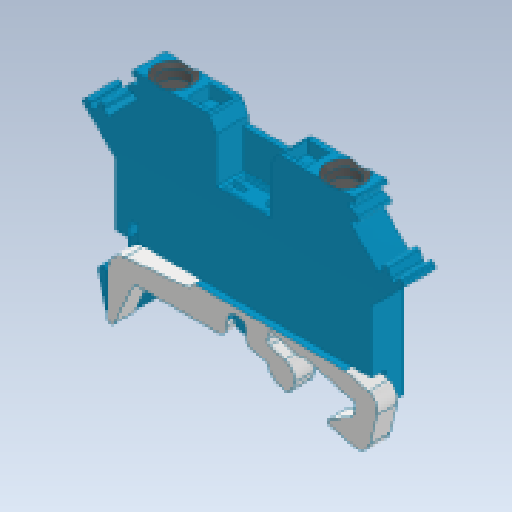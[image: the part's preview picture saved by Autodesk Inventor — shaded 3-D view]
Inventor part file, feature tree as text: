
AUTODESK INVENTOR PART (.ipt)
format: ipt  version: 2025.2 (Build 292293000, 293)  size: 807,424 bytes
history: native  units: mm
features: other x130, sketch x12, extrude x10, hole x2
ambient origin geometry x8: Origin, YZ Plane, XZ Plane, XY Plane, X Axis, Y Axis, Z Axis, Center Point
bodies: Solid1 (feature_tree)
feature tree (154):
  extrude  "Extrusion1"  Depth=2.1mm TaperAngle=0.0deg
  extrude  "Extrusion2"  Depth=2.0mm TaperAngle=0.0deg
  extrude  "Extrusion3"  Depth=7.0mm TaperAngle=0.0deg
  extrude  "Extrusion4"  Depth=5.0mm TaperAngle=0.0deg
  extrude  "Extrusion5"  Depth=3.6mm TaperAngle=0.0deg
  extrude  "Extrusion6"  TaperAngle=0.0deg  [1 undecoded]
  extrude  "Extrusion7"  TaperAngle=0.0deg  [1 undecoded]
  extrude  "Extrusion8"  TaperAngle=0.0deg  [1 undecoded]
  hole  "Hole1"  [1 undecoded]
  hole  "Hole2"  [1 undecoded]
  extrude  "Extrusion9"  Depth=10.0mm
  extrude  "Extrusion10"  Depth=10.0mm
  other  "1_2_XY"
  other  "1_2_YZ"
  other  "1_2_ZX"
  other  "1_2_X"
  other  "1_2_Y"
  other  "1_2_Z"
  other  "1_2_Center"
  other  "1_3_XY"
  other  "1_3_YZ"
  other  "1_3_ZX"
  other  "1_3_X"
  other  "1_3_Y"
  other  "1_3_Z"
  other  "1_3_Center"
  other  "1_4_XY"
  other  "1_4_YZ"
  other  "1_4_ZX"
  other  "1_4_X"
  other  "1_4_Y"
  other  "1_4_Z"
  other  "1_4_Center"
  other  "1_5_XY"
  other  "1_5_YZ"
  other  "1_5_ZX"
  other  "1_5_X"
  other  "1_5_Y"
  other  "1_5_Z"
  other  "1_5_Center"
  other  "1_6_XY"
  other  "1_6_YZ"
  other  "1_6_ZX"
  other  "1_6_X"
  other  "1_6_Y"
  other  "1_6_Z"
  other  "1_6_Center"
  other  "1_7_XY"
  other  "1_7_YZ"
  other  "1_7_ZX"
  other  "1_7_X"
  other  "1_7_Y"
  other  "1_7_Z"
  other  "1_7_Center"
  other  "1_8_XY"
  other  "1_8_YZ"
  other  "1_8_ZX"
  other  "1_8_X"
  other  "1_8_Y"
  other  "1_8_Z"
  other  "1_8_Center"
  other  "MD_XY"
  other  "MD_YZ"
  other  "MD_ZX"
  other  "MD_X"
  other  "MD_Y"
  other  "MD_Z"
  other  "MD_Center"
  other  "OP_XY"
  other  "OP_YZ"
  other  "OP_ZX"
  other  "OP_X"
  other  "OP_Y"
  other  "OP_Z"
  other  "OP_Center"
  other  "a1_XY"
  other  "a1_YZ"
  other  "a1_ZX"
  other  "a1_X"
  other  "a1_Y"
  other  "a1_Z"
  other  "a1_Center"
  other  "b2_XY"
  other  "b2_YZ"
  other  "b2_ZX"
  other  "b2_X"
  other  "b2_Y"
  other  "b2_Z"
  other  "b2_Center"
  other  "j3_XY"
  other  "j3_YZ"
  other  "j3_ZX"
  other  "j3_X"
  other  "j3_Y"
  other  "j3_Z"
  other  "j3_Center"
  other  "m4_XY"
  other  "m4_YZ"
  other  "m4_ZX"
  other  "m4_X"
  other  "m4_Y"
  other  "m4_Z"
  other  "m4_Center"
  other  "m5_XY"
  other  "m5_YZ"
  other  "m5_ZX"
  other  "m5_X"
  other  "m5_Y"
  other  "m5_Z"
  other  "m5_Center"
  other  "z6_XY"
  other  "z6_YZ"
  other  "z6_ZX"
  other  "z6_X"
  other  "z6_Y"
  other  "z6_Z"
  other  "z6_Center"
  other  "z7_XY"
  other  "z7_YZ"
  other  "z7_ZX"
  other  "z7_X"
  other  "z7_Y"
  other  "z7_Z"
  other  "z7_Center"
  other  "Edição direta1"
  other  "Edição direta2"
  other  "Edição direta3"
  other  "Edição direta4"
  other  "Edição direta5"
  other  "Edição direta6"
  other  "Edição direta7"
  other  "Edição direta8"
  other  "Edição direta9"
  sketch  "Skizze_1"  dims[d0=5.0mm d1=0.0mm d2=2.1mm d3=0.0mm]
  sketch  "Skizze_14"  dims[d39=0.0mm d40=0.0mm]
  sketch  "Skizze_15"  dims[d41=3.0mm d42=10.0mm d43=10.0mm d44=12.3mm d45=10.0mm d46=10.0mm]
  sketch  "Skizze_16"  dims[d47=12.0mm d48=10.0mm d49=10.0mm d50=0.25mm d51=0.55mm d52=-0.36mm d53=-0.4mm d54=0.0mm d55=0.0mm d56=0.0mm d57=0.0mm d58=0.35mm d59=0.5mm]
  sketch  "Skizze_2"  dims[d4=2.1mm d5=0.0mm d6=2.0mm d7=0.0mm]
  sketch  "Skizze_3"  dims[d8=0.8mm d9=0.0mm d10=7.0mm d11=0.0mm]
  sketch  "Skizze_4"  dims[d12=3.4mm d13=0.0mm d14=5.0mm d15=0.0mm]
  sketch  "Skizze_5"  dims[d16=4.2mm d17=6.0mm d18=5.8mm d19=2.0mm d20=18.545904mm d21=2.0mm d22=0.0mm]
  sketch  "Sketch9"  dims[d32=3.6mm d33=0.0mm d34=0.0mm]
  sketch  "Sketch10"  dims[d37=0.0mm d38=0.0mm]
  sketch  "Skizze_8"  dims[d23=4.2mm d24=6.0mm d25=5.8mm d26=2.0mm d27=18.545904mm d28=2.0mm d29=0.0mm d30=3.6mm d31=0.0mm]
  sketch  "Skizze_9"  dims[d35=0.0mm d36=0.0mm]
  other  "Escala1"
  other  "Escala2"
  other  "Escala3"
  other  "Tamanho1"
  other  "Tamanho2"
  other  "Tamanho3"
  other  "Mover1"
  other  "Mover2"
  other  "Tamanho4"
note: 5 required parameter values undecoded (feature->parameter linkage not recoverable at this tier; creation-order binding heuristic only, values carry confidence <= 0.55)
